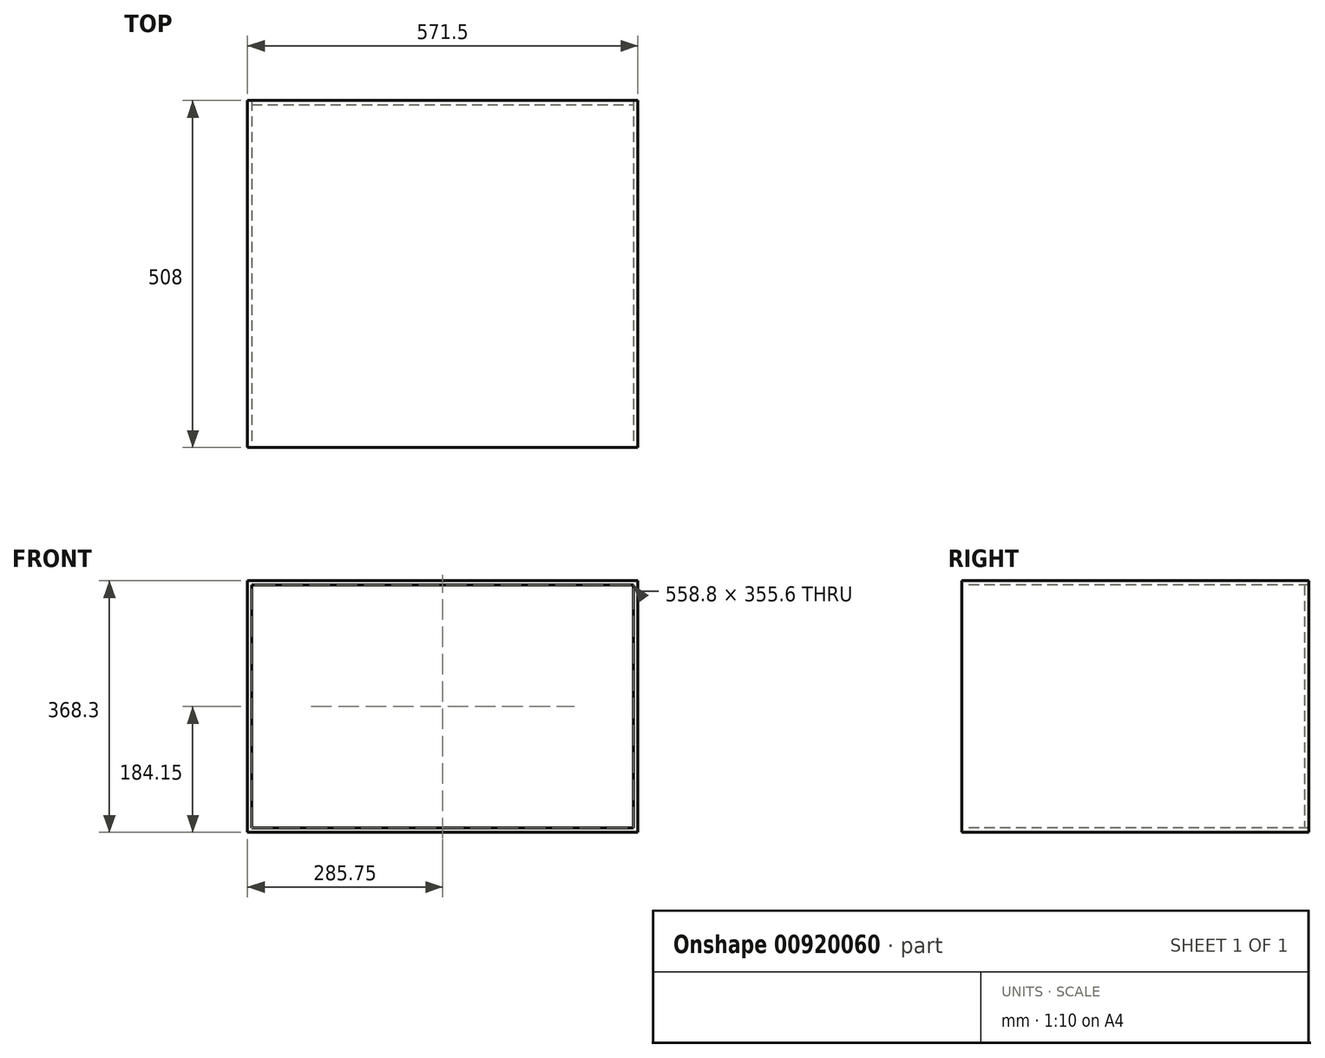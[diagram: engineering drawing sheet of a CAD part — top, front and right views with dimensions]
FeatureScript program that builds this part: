
annotation { "Feature Type Name" : "Feature", "Feature Type Description" : "" }
export const myFeature = defineFeature(function(context is Context, id is Id, definition is map)
    precondition{}
    {
        {
            var Q0;
            Q0=qCreatedBy(makeId("Front.planeOp"),FACE);
            var sketch = newSketch(context, id + "F0", { "sketchPlane" : qUnion([Q0])});
            skLineSegment(sketch, "E0.bottom", {"start": v(-285.75, 184.15) * mm, "end": v(285.75, 184.15) * mm});
            skLineSegment(sketch, "E0.top", {"start": v(-285.75, -184.15) * mm, "end": v(285.75, -184.15) * mm});
            skLineSegment(sketch, "E0.left", {"start": v(-285.75, 184.15) * mm, "end": v(-285.75, -184.15) * mm});
            skLineSegment(sketch, "E0.right", {"start": v(285.75, 184.15) * mm, "end": v(285.75, -184.15) * mm});
            skPoint(sketch, "E0.middle", {"position": v(0, 0) * mm});
            skLineSegment(sketch, "E1.0", {"start": v(-279.4, 177.8) * mm, "end": v(-279.4, -177.8) * mm});
            skLineSegment(sketch, "E1.1", {"start": v(-279.4, 177.8) * mm, "end": v(279.4, 177.8) * mm});
            skLineSegment(sketch, "E1.2", {"start": v(279.4, 177.8) * mm, "end": v(279.4, -177.8) * mm});
            skLineSegment(sketch, "E1.3", {"start": v(-279.4, -177.8) * mm, "end": v(279.4, -177.8) * mm});
            skSolve(sketch);
        }
        {
            var Q0;
            Q0=makeQuery(id+"F0.imprint","IMPRINT",FACE,{"disambiguationData":[TD([[makeQuery(id+"F0.imprint","IMPRINT",EDGE,{"derivedFrom":sQuery(id+"F0.wireOp",EDGE,"E0.bottom")}),-1.0]])]});
            extrude(context, id + "F1", {"entities" : qUnion([Q0]), "oppositeDirection" : true, "depth" : (25.4 * 20) * mm, "offsetDistance" : 25 * mm});
        }
        {
            var Q0;
            Q0=makeQuery(id+"F0.imprint","IMPRINT",FACE,{"disambiguationData":[TD([[makeQuery(id+"F0.imprint","IMPRINT",EDGE,{"derivedFrom":sQuery(id+"F0.wireOp",EDGE,"E1.0")}),1.0]])]});
            extrude(context, id + "F2", {"entities" : qUnion([Q0]), "depth" : (-25.4 * 20) * mm, "offsetDistance" : 25 * mm, "hasSecondDirection" : true, "secondDirectionOppositeDirection" : true, "secondDirectionDepth" : (508 - 6.35) * mm});
        }
    });
